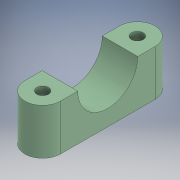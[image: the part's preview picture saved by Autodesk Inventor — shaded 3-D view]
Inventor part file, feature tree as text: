
AUTODESK INVENTOR PART (.ipt)
format: ipt  version: 2020 (Build 240168000, 168)  size: 153,088 bytes
history: native  units: mm
features: extrude x3, sketch x3, other x1
ambient origin geometry x8: Origin, YZ Plane, XZ Plane, XY Plane, X Axis, Y Axis, Z Axis, Center Point
bodies: Body1 (feature_tree)
feature tree (7):
  other  "Твердое тело1"
  extrude  "Выдавливание1"  Depth=15.0mm
  extrude  "Выдавливание2"  Depth=44.0mm
  extrude  "Выдавливание3"  Depth=16.0mm
  sketch  "Эскиз1"
  sketch  "Эскиз2"
  sketch  "Эскиз4"
